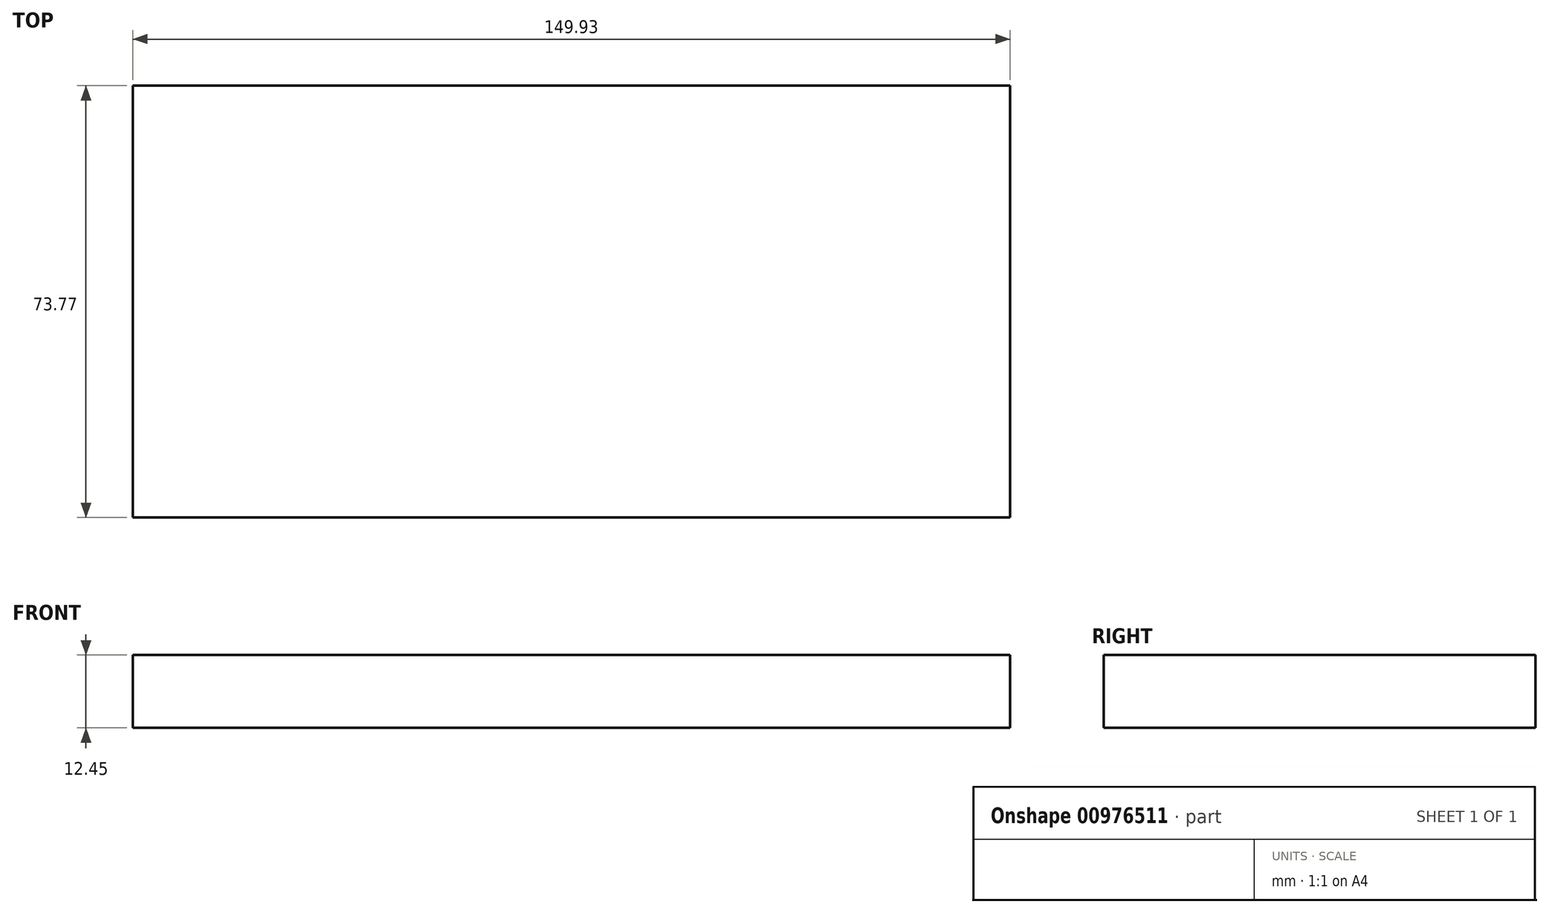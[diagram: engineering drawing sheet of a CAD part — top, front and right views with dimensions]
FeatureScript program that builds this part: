
annotation { "Feature Type Name" : "Feature", "Feature Type Description" : "" }
export const myFeature = defineFeature(function(context is Context, id is Id, definition is map)
    precondition{}
    {
        {
            var Q0;
            Q0=qCreatedBy(makeId("Top.planeOp"),FACE);
            var sketch = newSketch(context, id + "F0", { "sketchPlane" : qUnion([Q0])});
            skLineSegment(sketch, "E0.bottom", {"start": v(-49.55, 29.02) * mm, "end": v(100.38, 29.02) * mm});
            skLineSegment(sketch, "E0.top", {"start": v(-49.55, -44.75) * mm, "end": v(100.38, -44.75) * mm});
            skLineSegment(sketch, "E0.left", {"start": v(-49.55, 29.02) * mm, "end": v(-49.55, -44.75) * mm});
            skLineSegment(sketch, "E0.right", {"start": v(100.38, 29.02) * mm, "end": v(100.38, -44.75) * mm});
            skSolve(sketch);
        }
        {
            var Q0;
            Q0 = qSketchRegion(id + "F0", true);
            extrude(context, id + "F1", {"entities" : qUnion([Q0]), "depth" : 12.45 * mm, "offsetDistance" : 25.4 * mm});
        }
    });
